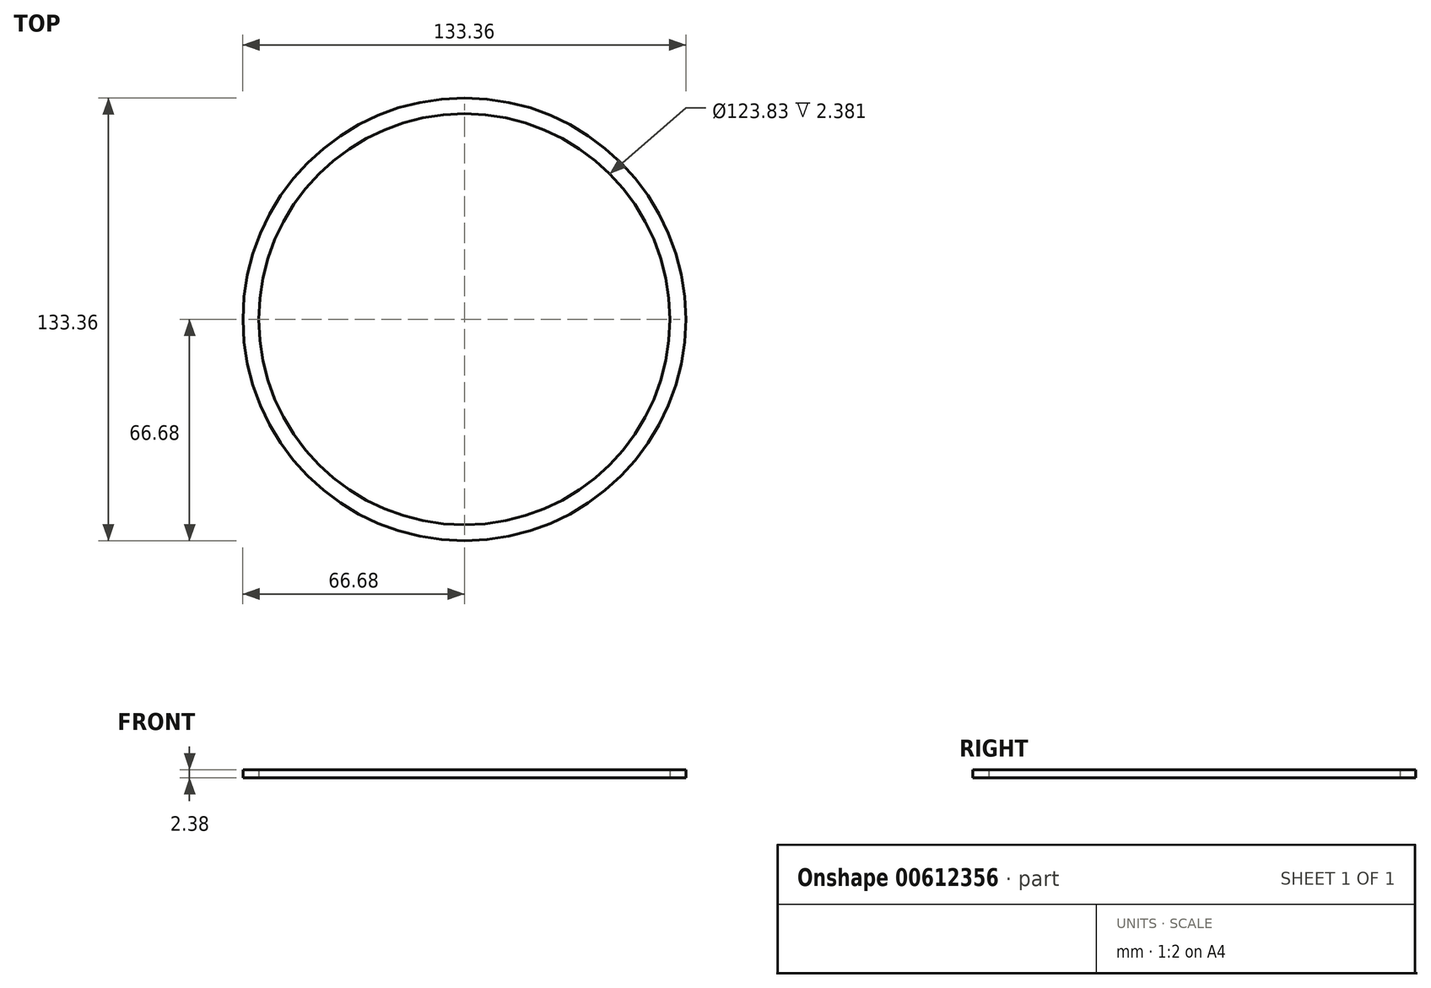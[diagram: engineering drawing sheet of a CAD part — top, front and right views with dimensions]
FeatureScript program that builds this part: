
annotation { "Feature Type Name" : "Feature", "Feature Type Description" : "" }
export const myFeature = defineFeature(function(context is Context, id is Id, definition is map)
    precondition{}
    {
        {
            var Q0;
            Q0=qCreatedBy(makeId("Front.planeOp"),FACE);
            var sketch = newSketch(context, id + "F0", { "sketchPlane" : qUnion([Q0])});
            skLineSegment(sketch, "E0.bottom", {"start": v(61.91, 0) * mm, "end": v(66.67, 0) * mm});
            skLineSegment(sketch, "E0.top", {"start": v(61.91, 2.38) * mm, "end": v(66.67, 2.38) * mm});
            skLineSegment(sketch, "E0.left", {"start": v(61.91, 0) * mm, "end": v(61.91, 2.38) * mm});
            skLineSegment(sketch, "E0.right", {"start": v(66.67, 0) * mm, "end": v(66.67, 2.38) * mm});
            skLineSegment(sketch, "E1", {"start": v(0, 0) * mm, "end": v(0, 18.18) * mm});
            skSolve(sketch);
        }
        {
            var Q0;
            Q0=makeQuery(id+"F0.imprint","IMPRINT",FACE,{"disambiguationData":[TD([[makeQuery(id+"F0.imprint","IMPRINT",EDGE,{"derivedFrom":sQuery(id+"F0.wireOp",EDGE,"E0.bottom")}),1.0]])]});
            var Q1;
            Q1=sQuery(id+"F0.wireOp",EDGE,"E1");
            revolve(context, id + "F1", {"entities" : qUnion([Q0]), "axis" : qUnion([Q1]), "revolveType" : RevolveType.FULL});
        }
    });
